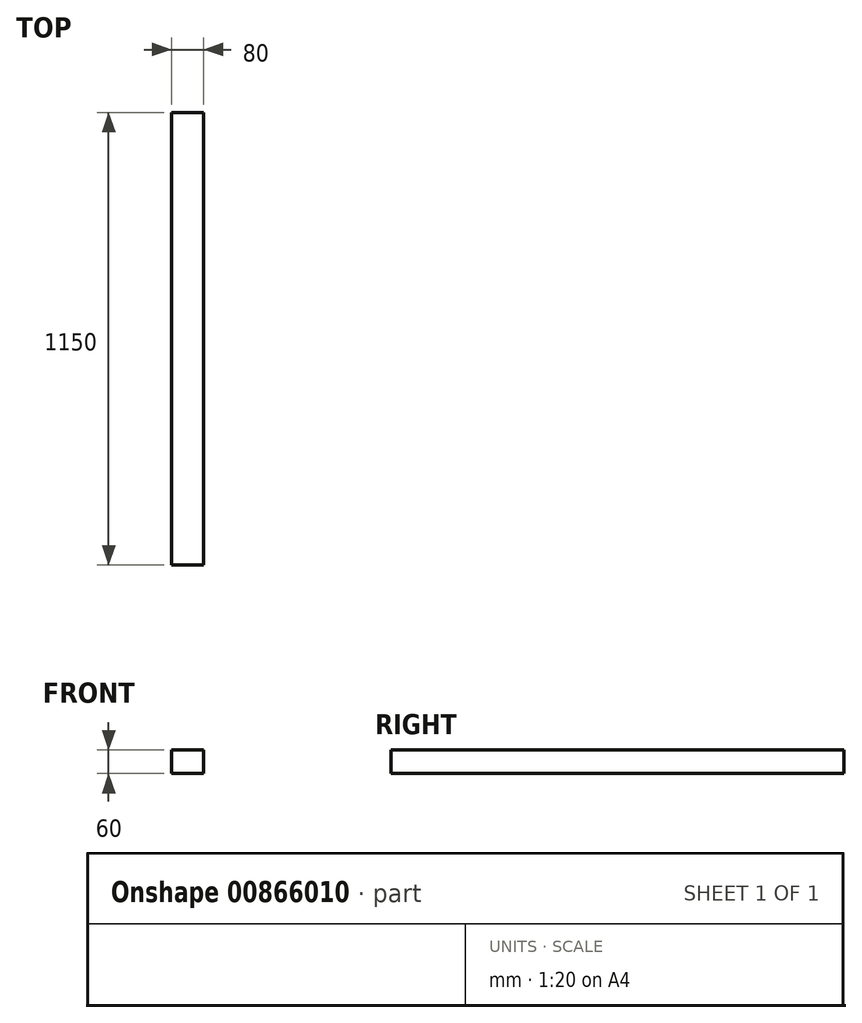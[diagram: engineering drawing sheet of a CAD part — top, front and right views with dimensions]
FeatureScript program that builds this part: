
annotation { "Feature Type Name" : "Feature", "Feature Type Description" : "" }
export const myFeature = defineFeature(function(context is Context, id is Id, definition is map)
    precondition{}
    {
        {
            var Q0;
            Q0=qCreatedBy(makeId("Front.planeOp"),FACE);
            var sketch = newSketch(context, id + "F0", { "sketchPlane" : qUnion([Q0])});
            skLineSegment(sketch, "E0.bottom", {"start": v(0, 0) * mm, "end": v(-80, 0) * mm});
            skLineSegment(sketch, "E0.top", {"start": v(0, 60) * mm, "end": v(-80, 60) * mm});
            skLineSegment(sketch, "E0.left", {"start": v(0, 0) * mm, "end": v(0, 60) * mm});
            skLineSegment(sketch, "E0.right", {"start": v(-80, 0) * mm, "end": v(-80, 60) * mm});
            skSolve(sketch);
        }
        {
            var Q0;
            Q0 = qSketchRegion(id + "F0", true);
            extrude(context, id + "F1", {"entities" : qUnion([Q0]), "depth" : 1150 * mm, "offsetDistance" : 25 * mm});
        }
    });
